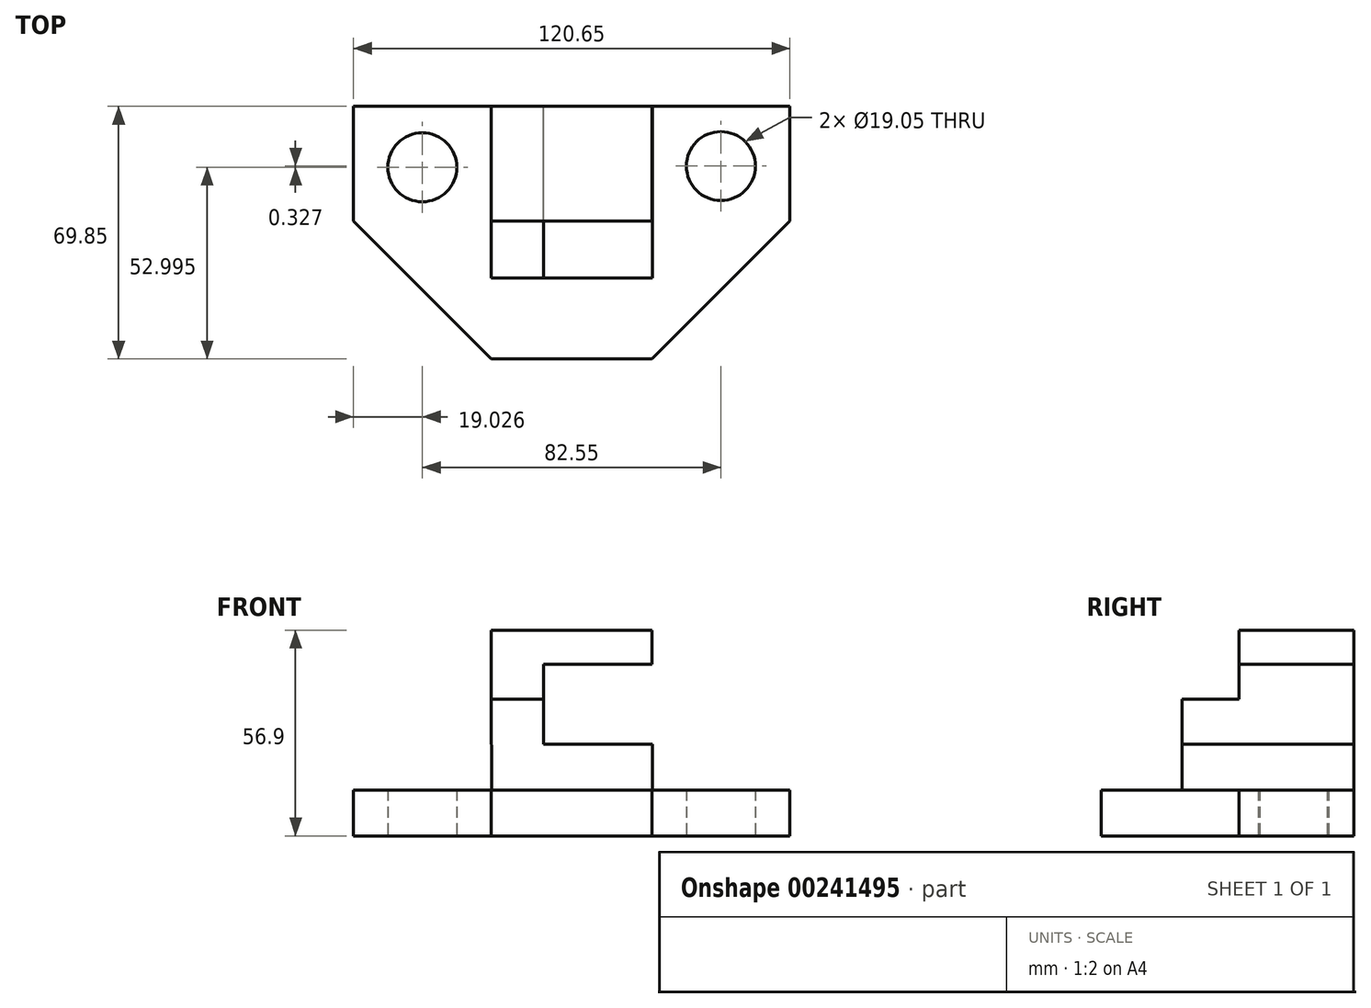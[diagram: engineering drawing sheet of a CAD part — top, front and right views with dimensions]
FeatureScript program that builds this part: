
annotation { "Feature Type Name" : "Feature", "Feature Type Description" : "" }
export const myFeature = defineFeature(function(context is Context, id is Id, definition is map)
    precondition{}
    {
        {
            var Q0;
            Q0=qCreatedBy(makeId("Top.planeOp"),FACE);
            var sketch = newSketch(context, id + "F0", { "sketchPlane" : qUnion([Q0])});
            skLineSegment(sketch, "E0", {"start": v(-52.5, 0) * mm, "end": v(68.16, 0) * mm});
            skLineSegment(sketch, "E1", {"start": v(-52.5, 0) * mm, "end": v(-52.5, -31.75) * mm});
            skLineSegment(sketch, "E2", {"start": v(68.16, 0) * mm, "end": v(68.16, -31.75) * mm});
            skLineSegment(sketch, "E3", {"start": v(-52.5, -31.75) * mm, "end": v(-14.4, -69.85) * mm});
            skLineSegment(sketch, "E4", {"start": v(68.16, -31.75) * mm, "end": v(30.06, -69.85) * mm});
            skLineSegment(sketch, "E5", {"start": v(-14.4, -69.85) * mm, "end": v(30.06, -69.85) * mm});
            skCircle(sketch, "E6", {"center": v(-33.46, -16.85) * mm, "radius": 9.53 * mm});
            skCircle(sketch, "E7", {"center": v(49.09, -16.53) * mm, "radius": 9.53 * mm});
            skSolve(sketch);
        }
        {
            var Q0;
            Q0=makeQuery(id+"F0.imprint","IMPRINT",FACE,{"disambiguationData":[TD([[makeQuery(id+"F0.imprint","IMPRINT",EDGE,{"derivedFrom":sQuery(id+"F0.wireOp",EDGE,"E0")}),-1.0]])]});
            var Q1;
            Q1 = qSketchRegion(id + "F2", true);
            extrude(context, id + "F1", {"entities" : qUnion([Q0, Q1]), "offsetDistance" : 25.4 * mm, "depth" : 12.7 * mm});
        }
        {
            var Q0;
            Q0=qCreatedBy(makeId("Front.planeOp"),FACE);
            var sketch = newSketch(context, id + "F2", { "sketchPlane" : qUnion([Q0])});
            skLineSegment(sketch, "E8", {"start": v(-14.34, 0) * mm, "end": v(30.1, 0) * mm});
            skLineSegment(sketch, "E9", {"start": v(30.1, 0) * mm, "end": v(30.1, 25.4) * mm});
            skLineSegment(sketch, "E10", {"start": v(30.1, 25.4) * mm, "end": v(0, 25.4) * mm});
            skLineSegment(sketch, "E11", {"start": v(0, 25.4) * mm, "end": v(0, 37.85) * mm});
            skLineSegment(sketch, "E12", {"start": v(0, 37.85) * mm, "end": v(-14.4, 37.85) * mm});
            skLineSegment(sketch, "E13", {"start": v(-14.4, 37.85) * mm, "end": v(-14.34, 0) * mm});
            skLineSegment(sketch, "E14", {"start": v(0, 37.85) * mm, "end": v(0, 47.5) * mm});
            skLineSegment(sketch, "E15", {"start": v(0, 47.5) * mm, "end": v(30.05, 47.5) * mm});
            skLineSegment(sketch, "E16", {"start": v(30.05, 47.5) * mm, "end": v(30.05, 56.9) * mm});
            skLineSegment(sketch, "E17", {"start": v(30.05, 56.9) * mm, "end": v(-14.4, 56.9) * mm});
            skLineSegment(sketch, "E18", {"start": v(-14.4, 56.9) * mm, "end": v(-14.4, 37.85) * mm});
            skSolve(sketch);
        }
        {
            var Q0;
            Q0=makeQuery(id+"F2.imprint","IMPRINT",FACE,{"disambiguationData":[TD([[makeQuery(id+"F2.imprint","IMPRINT",EDGE,{"derivedFrom":sQuery(id+"F2.wireOp",EDGE,"E8")}),1.0]])]});
            extrude(context, id + "F3", {"entities" : qUnion([Q0]), "operationType" : NewBodyOperationType.ADD, "depth" : 47.5 * mm});
        }
        {
            var Q0;
            Q0=makeQuery(id+"F2.imprint","IMPRINT",FACE,{"disambiguationData":[TD([[makeQuery(id+"F2.imprint","IMPRINT",EDGE,{"derivedFrom":sQuery(id+"F2.wireOp",EDGE,"E12")}),-1.0]])]});
            extrude(context, id + "F4", {"entities" : qUnion([Q0]), "operationType" : NewBodyOperationType.ADD, "depth" : 31.75 * mm});
        }
    });
